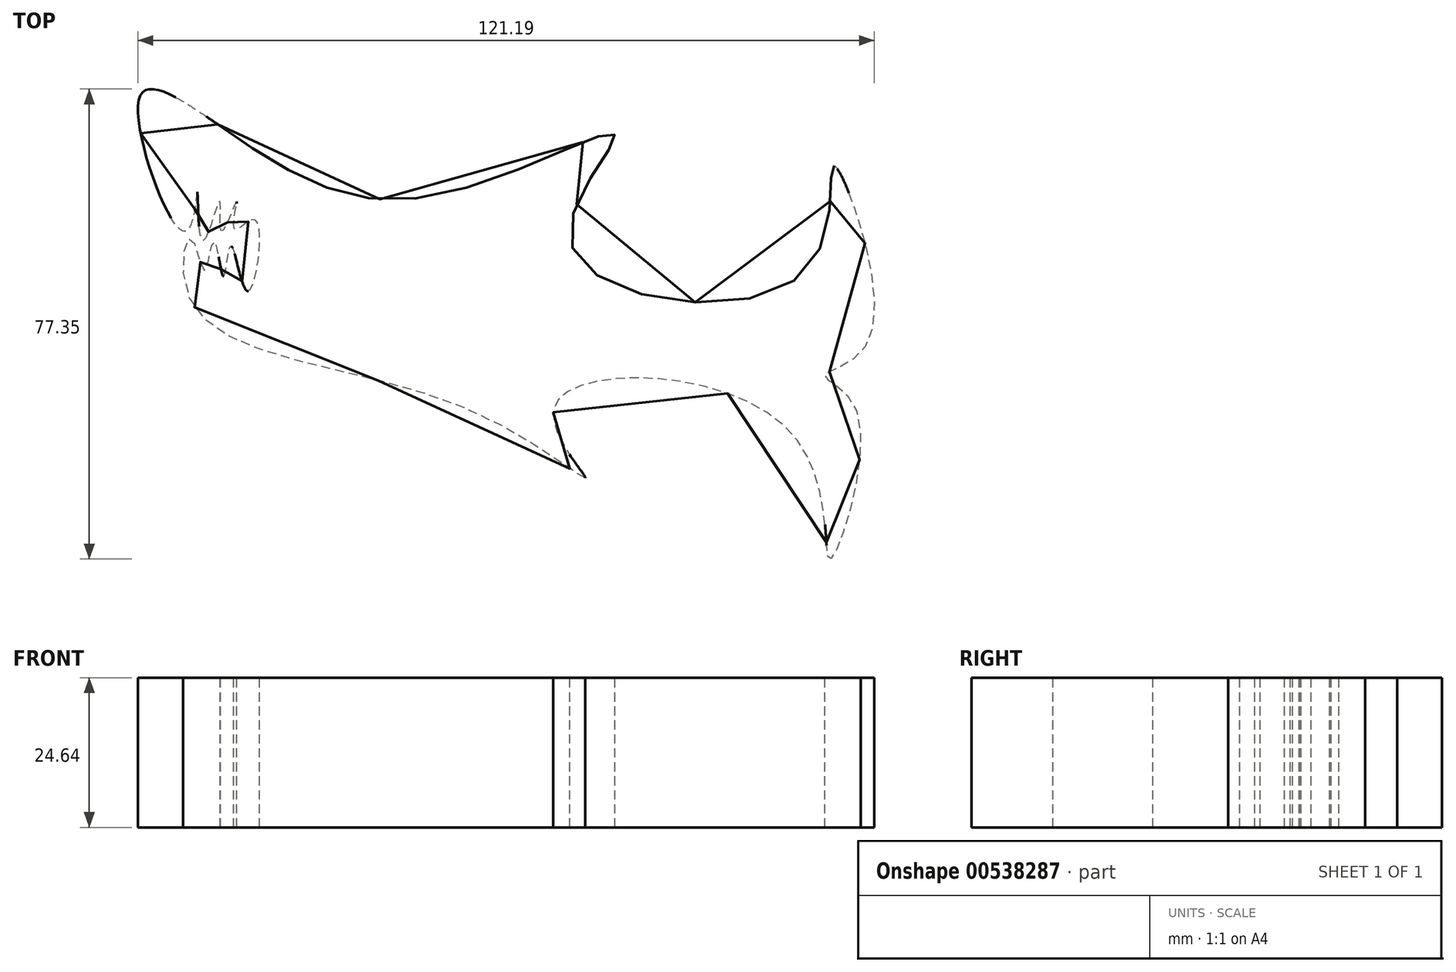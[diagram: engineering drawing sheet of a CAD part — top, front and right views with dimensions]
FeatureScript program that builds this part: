
annotation { "Feature Type Name" : "Feature", "Feature Type Description" : "" }
export const myFeature = defineFeature(function(context is Context, id is Id, definition is map)
    precondition{}
    {
        {
            var Q0;
            Q0=qCreatedBy(makeId("Top.planeOp"),FACE);
            var sketch = newSketch(context, id + "F0", { "sketchPlane" : qUnion([Q0])});
            skFitSpline(sketch, "E0", {"points": [v(-49.81, 50.69) * mm, v(-15.91, 38.67) * mm, v(15.52, 48.84) * mm, v(8.43, 30.66) * mm, v(46.65, 26.34) * mm, v(51.58, 43.9) * mm, v(57.44, 15.55) * mm, v(50.04, 9.4) * mm, v(55.28, 3.54) * mm, v(50.96, -20.81) * mm, v(44.5, 0) * mm, v(5.66, 4.46) * mm, v(10.6, -7.25) * mm, v(-9.44, 4.15) * mm, v(-54.13, 21.41) * mm, v(-54.13, 31.89) * mm, v(-51.97, 26.65) * mm, v(-50.43, 31.58) * mm, v(-48.89, 25.73) * mm, v(-47.66, 30.66) * mm, v(-44.88, 23.26) * mm, v(-43.65, 34.97) * mm, v(-47.04, 33.43) * mm, v(-46.73, 38.05) * mm, v(-49.2, 33.12) * mm, v(-49.5, 38.05) * mm, v(-52.28, 31.58) * mm, v(-53.2, 39.6) * mm, v(-55.05, 33.12) * mm, v(-62.76, 55) * mm, v(-49.81, 50.69) * mm]});
            skSolve(sketch);
        }
        {
            var Q0;
            Q0=makeQuery(id+"F0.imprint","IMPRINT",FACE,{"disambiguationData":[TD([[makeQuery(id+"F0.imprint","IMPRINT",EDGE,{"derivedFrom":sQuery(id+"F0.wireOp",EDGE,"E0")}),-1.0]])]});
            extrude(context, id + "F1", {"entities" : qUnion([Q0]), "oppositeDirection" : true, "depth" : 24.64 * mm, "offsetDistance" : 25.4 * mm});
        }
        {
            var Q0;
            Q0=makeQuery(id+"F1.opExtrude","CAP_FACE",FACE,{"disambiguationData":[OSD([sQuery(id+"F0.wireOp",EDGE,"E0")])],"isStart":true});
            var sketch = newSketch(context, id + "F2", { "sketchPlane" : qUnion([Q0])});
            skCircle(sketch, "E1", {"center": v(-34.71, 34.97) * mm, "radius": 2.47 * mm});
            skSolve(sketch);
        }
        {
            var Q0;
            Q0=makeQuery(id+"F2.imprint","IMPRINT",FACE,{"disambiguationData":[TD([[makeQuery(id+"F2.imprint","IMPRINT",EDGE,{"derivedFrom":sQuery(id+"F2.wireOp",EDGE,"E1")}),1.0]])]});
            extrude(context, id + "F3", {"entities" : qUnion([Q0]), "operationType" : NewBodyOperationType.REMOVE, "depth" : 100.08 * mm, "offsetDistance" : 25.4 * mm});
        }
    });
